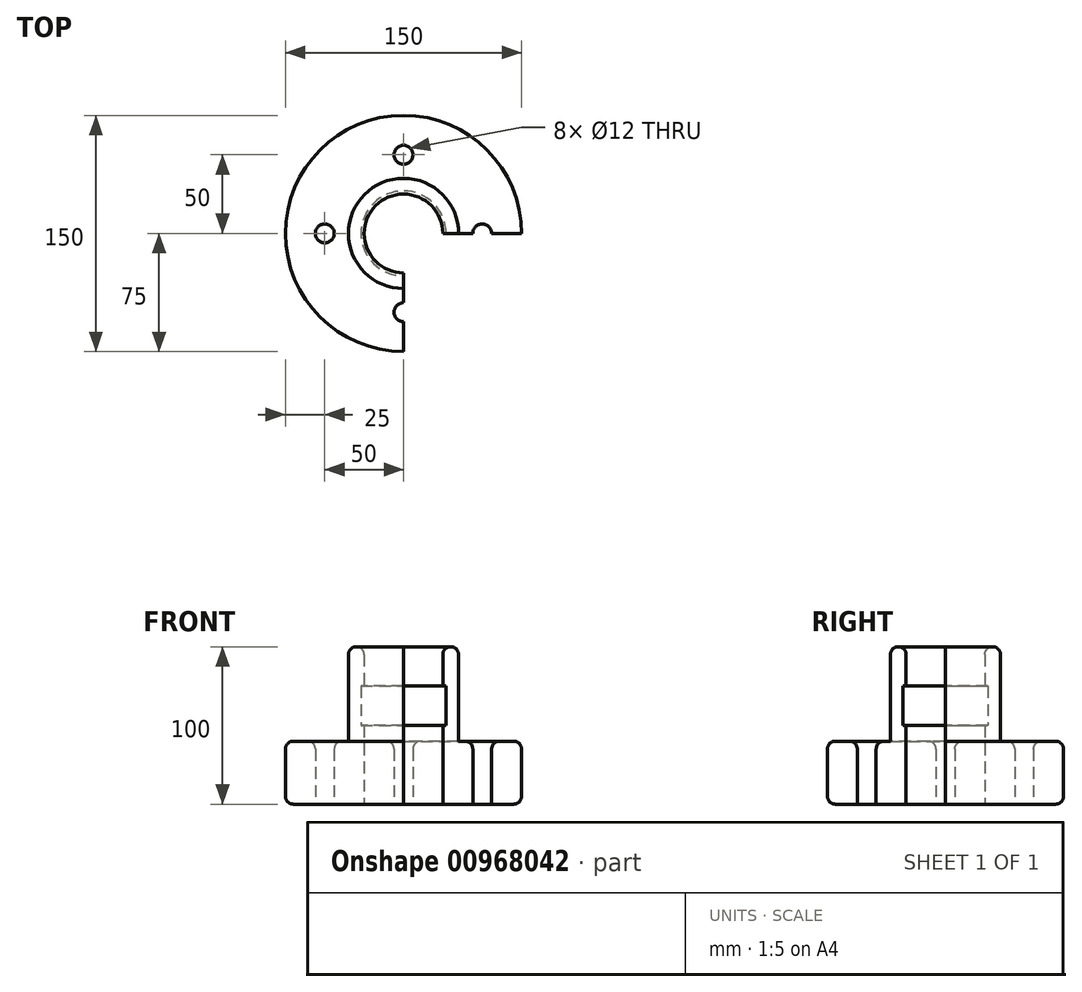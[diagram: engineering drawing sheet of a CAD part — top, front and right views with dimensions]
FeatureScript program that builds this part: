
annotation { "Feature Type Name" : "Feature", "Feature Type Description" : "" }
export const myFeature = defineFeature(function(context is Context, id is Id, definition is map)
    precondition{}
    {
        {
            var Q0;
            Q0=qCreatedBy(makeId("Front.planeOp"),FACE);
            var sketch = newSketch(context, id + "F0", { "sketchPlane" : qUnion([Q0])});
            skLineSegment(sketch, "E0", {"start": v(0, 0) * mm, "end": v(25, 0) * mm});
            skLineSegment(sketch, "E1", {"start": v(25, 0) * mm, "end": v(35, 0) * mm});
            skLineSegment(sketch, "E2", {"start": v(35, 0) * mm, "end": v(75, 0) * mm});
            skLineSegment(sketch, "E3", {"start": v(75, 0) * mm, "end": v(75, 40) * mm});
            skLineSegment(sketch, "E4", {"start": v(75, 40) * mm, "end": v(35, 40) * mm});
            skLineSegment(sketch, "E5", {"start": v(35, 40) * mm, "end": v(35, 100) * mm});
            skLineSegment(sketch, "E6", {"start": v(35, 100) * mm, "end": v(25, 100) * mm});
            skLineSegment(sketch, "E7", {"start": v(25, 100) * mm, "end": v(25, 75) * mm});
            skLineSegment(sketch, "E8", {"start": v(25, 75) * mm, "end": v(27, 75) * mm});
            skLineSegment(sketch, "E9", {"start": v(27, 75) * mm, "end": v(27, 50) * mm});
            skLineSegment(sketch, "E10", {"start": v(27, 50) * mm, "end": v(25, 50) * mm});
            skLineSegment(sketch, "E11", {"start": v(25, 50) * mm, "end": v(25, 0) * mm});
            skLineSegment(sketch, "E12", {"start": v(0, 0) * mm, "end": v(0, 72.12) * mm});
            skSolve(sketch);
        }
        {
            var Q0;
            Q0 = qSketchRegion(id + "F0", true);
            var Q1;
            Q1=sQuery(id+"F0.wireOp",EDGE,"E12");
            revolve(context, id + "F1", {"surfaceOperationType" : NewSurfaceOperationType.NEW, "entities" : qUnion([Q0]), "axis" : qUnion([Q1]), "revolveType" : RevolveType.ONE_DIRECTION, "angle" : 270 * degree});
        }
        {
            var Q0;
            Q0=qCreatedBy(makeId("Top.planeOp"),FACE);
            var sketch = newSketch(context, id + "F2", { "sketchPlane" : qUnion([Q0])});
            skCircle(sketch, "E13", {"center": v(0, 0) * mm, "radius": 50 * mm});
            skCircle(sketch, "E14", {"center": v(0, 50) * mm, "radius": 6 * mm});
            skCircle(sketch, "E15.1.0", {"center": v(-50, 0) * mm, "radius": 6 * mm});
            skCircle(sketch, "E15.2.0", {"center": v(0, -50) * mm, "radius": 6 * mm});
            skCircle(sketch, "E15.3.0", {"center": v(50, 0) * mm, "radius": 6 * mm});
            skSolve(sketch);
        }
        {
            var Q0;
            {var subQ0=sQuery(id+"F2.wireOp",EDGE,"E15.1.0");var subQ1=sQuery(id+"F2.wireOp",EDGE,"E13");var subQ2=makeQuery(id+"F2.imprint","INTERSECT",VERTEX,{"disambiguationData":[OD(0.0)],"derivedFrom":[subQ1,subQ0]});Q0=makeQuery(id+"F2.imprint","IMPRINT",FACE,{"disambiguationData":[TD([[makeQuery(id+"F2.imprint","IMPRINT",EDGE,{"disambiguationData":[TD([[subQ2,-1.0]])],"derivedFrom":subQ1}),1.0]])]});}
            var Q1;
            {var subQ0=sQuery(id+"F2.wireOp",EDGE,"E15.1.0");var subQ1=sQuery(id+"F2.wireOp",EDGE,"E13");var subQ2=makeQuery(id+"F2.imprint","INTERSECT",VERTEX,{"disambiguationData":[OD(0.0)],"derivedFrom":[subQ1,subQ0]});Q1=makeQuery(id+"F2.imprint","IMPRINT",FACE,{"disambiguationData":[TD([[makeQuery(id+"F2.imprint","IMPRINT",EDGE,{"disambiguationData":[TD([[subQ2,-1.0]])],"derivedFrom":subQ1}),-1.0]])]});}
            var Q2;
            {var subQ0=sQuery(id+"F2.wireOp",EDGE,"E14");var subQ1=sQuery(id+"F2.wireOp",EDGE,"E13");var subQ2=makeQuery(id+"F2.imprint","INTERSECT",VERTEX,{"disambiguationData":[OD(0.0)],"derivedFrom":[subQ1,subQ0]});Q2=makeQuery(id+"F2.imprint","IMPRINT",FACE,{"disambiguationData":[TD([[makeQuery(id+"F2.imprint","IMPRINT",EDGE,{"disambiguationData":[TD([[subQ2,-1.0]])],"derivedFrom":subQ1}),1.0]])]});}
            var Q3;
            {var subQ0=sQuery(id+"F2.wireOp",EDGE,"E14");var subQ1=sQuery(id+"F2.wireOp",EDGE,"E13");var subQ2=makeQuery(id+"F2.imprint","INTERSECT",VERTEX,{"disambiguationData":[OD(0.0)],"derivedFrom":[subQ1,subQ0]});Q3=makeQuery(id+"F2.imprint","IMPRINT",FACE,{"disambiguationData":[TD([[makeQuery(id+"F2.imprint","IMPRINT",EDGE,{"disambiguationData":[TD([[subQ2,-1.0]])],"derivedFrom":subQ1}),-1.0]])]});}
            var Q4;
            {var subQ0=sQuery(id+"F2.wireOp",EDGE,"E15.3.0");var subQ1=sQuery(id+"F2.wireOp",EDGE,"E13");var subQ2=makeQuery(id+"F2.imprint","INTERSECT",VERTEX,{"disambiguationData":[OD(0.0)],"derivedFrom":[subQ1,subQ0]});Q4=makeQuery(id+"F2.imprint","IMPRINT",FACE,{"disambiguationData":[TD([[makeQuery(id+"F2.imprint","IMPRINT",EDGE,{"disambiguationData":[TD([[subQ2,1.0]])],"derivedFrom":subQ1}),1.0]])]});}
            var Q5;
            {var subQ0=sQuery(id+"F2.wireOp",EDGE,"E15.3.0");var subQ1=sQuery(id+"F2.wireOp",EDGE,"E13");var subQ2=makeQuery(id+"F2.imprint","INTERSECT",VERTEX,{"disambiguationData":[OD(0.0)],"derivedFrom":[subQ1,subQ0]});Q5=makeQuery(id+"F2.imprint","IMPRINT",FACE,{"disambiguationData":[TD([[makeQuery(id+"F2.imprint","IMPRINT",EDGE,{"disambiguationData":[TD([[subQ2,1.0]])],"derivedFrom":subQ1}),-1.0]])]});}
            var Q6;
            {var subQ0=sQuery(id+"F2.wireOp",EDGE,"E15.2.0");var subQ1=sQuery(id+"F2.wireOp",EDGE,"E13");var subQ2=makeQuery(id+"F2.imprint","INTERSECT",VERTEX,{"disambiguationData":[OD(0.0)],"derivedFrom":[subQ1,subQ0]});Q6=makeQuery(id+"F2.imprint","IMPRINT",FACE,{"disambiguationData":[TD([[makeQuery(id+"F2.imprint","IMPRINT",EDGE,{"disambiguationData":[TD([[subQ2,-1.0]])],"derivedFrom":subQ1}),1.0]])]});}
            var Q7;
            {var subQ0=sQuery(id+"F2.wireOp",EDGE,"E15.2.0");var subQ1=sQuery(id+"F2.wireOp",EDGE,"E13");var subQ2=makeQuery(id+"F2.imprint","INTERSECT",VERTEX,{"disambiguationData":[OD(0.0)],"derivedFrom":[subQ1,subQ0]});Q7=makeQuery(id+"F2.imprint","IMPRINT",FACE,{"disambiguationData":[TD([[makeQuery(id+"F2.imprint","IMPRINT",EDGE,{"disambiguationData":[TD([[subQ2,-1.0]])],"derivedFrom":subQ1}),-1.0]])]});}
            extrude(context, id + "F3", {"entities" : qUnion([Q0, Q1, Q2, Q3, Q4, Q5, Q6, Q7]), "operationType" : NewBodyOperationType.REMOVE, "depth" : 1000 * mm, "offsetDistance" : 25 * mm});
        }
        {
            var Q0;
            Q0=makeQuery(id+"F1.opRevolve","SWEPT_EDGE",EDGE,{"disambiguationData":[OSD([sQuery(id+"F0.wireOp",EDGE,"E5"),sQuery(id+"F0.wireOp",EDGE,"E6")])]});
            var Q1;
            Q1=makeQuery(id+"F1.opRevolve","SWEPT_EDGE",EDGE,{"disambiguationData":[OSD([sQuery(id+"F0.wireOp",EDGE,"E6"),sQuery(id+"F0.wireOp",EDGE,"E7")])]});
            var Q2;
            Q2=makeQuery(id+"F1.opRevolve","SWEPT_EDGE",EDGE,{"disambiguationData":[OSD([sQuery(id+"F0.wireOp",EDGE,"E3"),sQuery(id+"F0.wireOp",EDGE,"E4")])]});
            var Q3;
            Q3=makeQuery(id+"F3.boolean.opBoolean","INTERSECT",EDGE,{"derivedFrom":[makeQuery(id+"F1.opRevolve","SWEPT_FACE",FACE,{"disambiguationData":[OSD([sQuery(id+"F0.wireOp",EDGE,"E4")])]}),makeQuery(id+"F3.opExtrude","SWEPT_FACE",FACE,{"disambiguationData":[OSD([sQuery(id+"F2.wireOp",EDGE,"E15.1.0")])]})]});
            var Q4;
            Q4=makeQuery(id+"F3.boolean.opBoolean","INTERSECT",EDGE,{"derivedFrom":[makeQuery(id+"F1.opRevolve","SWEPT_FACE",FACE,{"disambiguationData":[OSD([sQuery(id+"F0.wireOp",EDGE,"E4")])]}),makeQuery(id+"F3.opExtrude","SWEPT_FACE",FACE,{"disambiguationData":[OSD([sQuery(id+"F2.wireOp",EDGE,"E15.2.0")])]})]});
            var Q5;
            Q5=makeQuery(id+"F3.boolean.opBoolean","INTERSECT",EDGE,{"derivedFrom":[makeQuery(id+"F1.opRevolve","SWEPT_FACE",FACE,{"disambiguationData":[OSD([sQuery(id+"F0.wireOp",EDGE,"E4")])]}),makeQuery(id+"F3.opExtrude","SWEPT_FACE",FACE,{"disambiguationData":[OSD([sQuery(id+"F2.wireOp",EDGE,"E15.3.0")])]})]});
            var Q6;
            Q6=makeQuery(id+"F3.boolean.opBoolean","INTERSECT",EDGE,{"derivedFrom":[makeQuery(id+"F1.opRevolve","SWEPT_FACE",FACE,{"disambiguationData":[OSD([sQuery(id+"F0.wireOp",EDGE,"E4")])]}),makeQuery(id+"F3.opExtrude","SWEPT_FACE",FACE,{"disambiguationData":[OSD([sQuery(id+"F2.wireOp",EDGE,"E14")])]})]});
            var Q7;
            Q7=makeQuery(id+"F1.opRevolve","SWEPT_EDGE",EDGE,{"disambiguationData":[OSD([sQuery(id+"F0.wireOp",EDGE,"E2"),sQuery(id+"F0.wireOp",EDGE,"E3")])]});
            fillet(context, id + "F4", {"entities" : qUnion([Q0, Q1, Q2, Q3, Q4, Q5, Q6, Q7]), "radius" : 5 * mm, "tangentPropagation" : true, "allowEdgeOverflow" : false});
        }
    });
